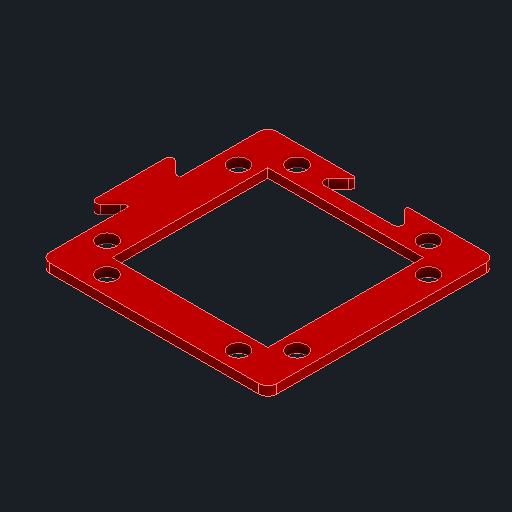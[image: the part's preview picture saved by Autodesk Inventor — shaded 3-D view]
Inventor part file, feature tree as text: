
AUTODESK INVENTOR PART (.ipt)
format: ipt  version: 2023.4 (Build 274418000, 418)  size: 387,584 bytes
history: native  units: mm
features: reference x9, extrude x3, other x3, sketch x2, fillet x1, projected_geometry x1
ambient origin geometry x8: Origin, YZ Plane, XZ Plane, XY Plane, X Axis, Y Axis, Z Axis, Center Point
bodies: Solid1 (feature_tree)
feature tree (19):
  extrude  "Extrusion1"  Depth=2.0mm TaperAngle=0.0deg
  sketch  "Sketch2"  dims[d16=10.0mm d17=0.0mm d18=0.25mm d19=20.0mm d20=10.0mm d21=45.0deg d22=1.0mm d23=1.5mm d24=1.0mm d25=0.075mm d28=15.171573mm d29=2.87868mm d30=2.87868mm d31=20.0mm d32=10.0mm d33=45.0deg d34=1.0mm d35=1.5mm d36=1.0mm d37=0.075mm d38=15.171573mm d39=2.87868mm d40=2.87868mm d41=0.25mm d42=0.0mm d43=40.0mm d45=360.0deg]
  extrude  "Extrusion2"  Depth=0.25mm
  extrude  "Extrusion3"  Depth=0.25mm
  fillet  "Fillet1"  Radius=2.87868mm
  sketch  "Sketch1"  dims[d0=2.0mm d1=0.0mm d14=2.0mm d15=0.0mm]
  reference  "Reference1"
  reference  "Reference2"
  reference  "Reference3"
  reference  "Reference4"
  reference  "Reference5"
  reference  "Reference6"
  reference  "Reference7"
  reference  "Reference8"
  reference  "Reference9"
  projected_geometry  "Projected Loop2"
  other  "<path>\Projects\Project Protocube\Protocube\CAD, STL, OBJ Files\1 CAD\Cube 1x1 V5.iam"
  other  "Cube 1x1 V5.iam"
  other  "Cube 1x1 Top V5:1"
note: 1 file-system path scrubbed to <path> (originals preserved in map.json)
